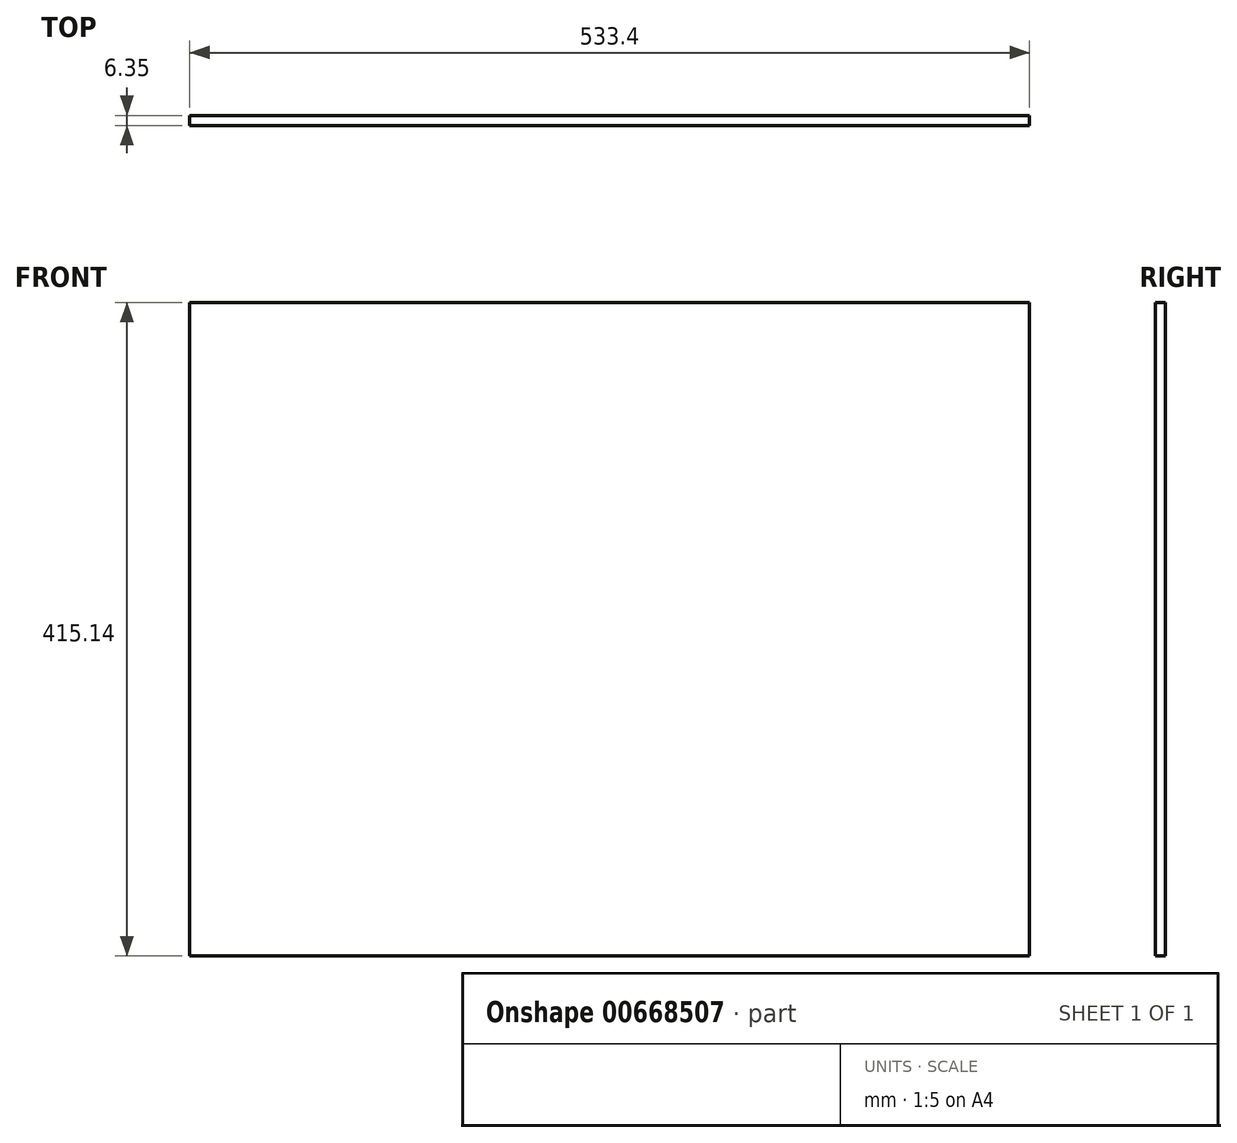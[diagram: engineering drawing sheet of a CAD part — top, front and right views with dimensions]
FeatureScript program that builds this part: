
annotation { "Feature Type Name" : "Feature", "Feature Type Description" : "" }
export const myFeature = defineFeature(function(context is Context, id is Id, definition is map)
    precondition{}
    {
        {
            var Q0;
            Q0=qCreatedBy(makeId("Front.planeOp"),FACE);
            var sketch = newSketch(context, id + "F0", { "sketchPlane" : qUnion([Q0])});
            skLineSegment(sketch, "E0.bottom", {"start": v(-266.7, -207.57) * mm, "end": v(266.7, -207.57) * mm});
            skLineSegment(sketch, "E0.top", {"start": v(-266.7, 207.57) * mm, "end": v(266.7, 207.57) * mm});
            skLineSegment(sketch, "E0.left", {"start": v(-266.7, -207.57) * mm, "end": v(-266.7, 207.57) * mm});
            skLineSegment(sketch, "E0.right", {"start": v(266.7, -207.57) * mm, "end": v(266.7, 207.57) * mm});
            skPoint(sketch, "E0.middle", {"position": v(0, 0) * mm});
            skSolve(sketch);
        }
        {
            var Q0;
            Q0 = qSketchRegion(id + "F0", true);
            extrude(context, id + "F1", {"entities" : qUnion([Q0]), "depth" : 6.35 * mm, "offsetDistance" : 25.4 * mm});
        }
    });
